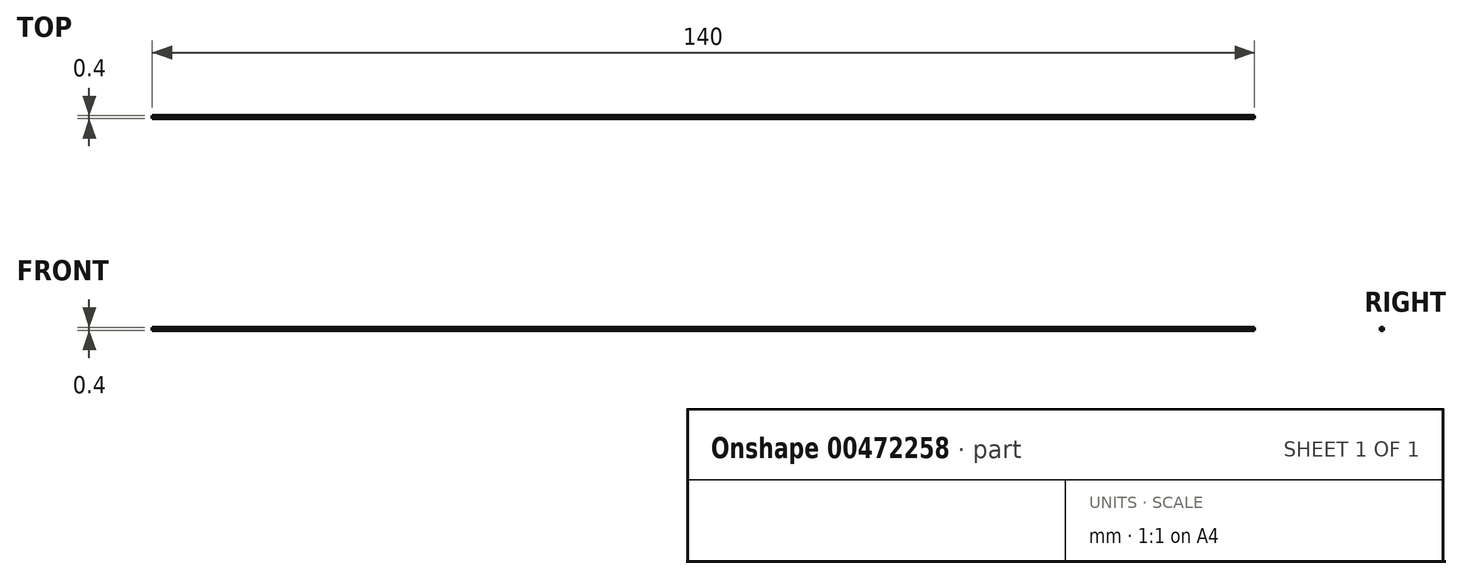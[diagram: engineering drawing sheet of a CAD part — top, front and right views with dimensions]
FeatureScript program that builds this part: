
annotation { "Feature Type Name" : "Feature", "Feature Type Description" : "" }
export const myFeature = defineFeature(function(context is Context, id is Id, definition is map)
    precondition{}
    {
        {
            var Q0;
            Q0=qCreatedBy(makeId("Top.planeOp"),FACE);
            var sketch = newSketch(context, id + "F0", { "sketchPlane" : qUnion([Q0])});
            skLineSegment(sketch, "E0.bottom", {"start": v(70, -0.2) * mm, "end": v(-70, -0.2) * mm});
            skLineSegment(sketch, "E0.top", {"start": v(70, 0.2) * mm, "end": v(-70, 0.2) * mm});
            skLineSegment(sketch, "E0.left", {"start": v(70, -0.2) * mm, "end": v(70, 0.2) * mm});
            skLineSegment(sketch, "E0.right", {"start": v(-70, -0.2) * mm, "end": v(-70, 0.2) * mm});
            skPoint(sketch, "E0.middle", {"position": v(0, 0) * mm});
            skLineSegment(sketch, "E1", {"start": v(70, -0.2) * mm, "end": v(70, -4.81) * mm});
            skLineSegment(sketch, "E2", {"start": v(70, -4.81) * mm, "end": v(72.97, -4.81) * mm});
            skLineSegment(sketch, "E3", {"start": v(72.97, -4.81) * mm, "end": v(72.97, 5.53) * mm});
            skLineSegment(sketch, "E4", {"start": v(72.97, 5.53) * mm, "end": v(70, 5.53) * mm});
            skLineSegment(sketch, "E5", {"start": v(70, 5.53) * mm, "end": v(70, 0.2) * mm});
            skLineSegment(sketch, "E6", {"start": v(-70, -0.2) * mm, "end": v(-70, -3.83) * mm});
            skLineSegment(sketch, "E7", {"start": v(-70, -3.83) * mm, "end": v(-74.12, -3.83) * mm});
            skLineSegment(sketch, "E8", {"start": v(-74.12, -3.83) * mm, "end": v(-74.12, 4.86) * mm});
            skLineSegment(sketch, "E9", {"start": v(-74.12, 4.86) * mm, "end": v(-70, 4.86) * mm});
            skLineSegment(sketch, "E10", {"start": v(-70, 4.86) * mm, "end": v(-70, 0.2) * mm});
            skSolve(sketch);
        }
        {
            var Q0;
            Q0=makeQuery(id+"F0.imprint","IMPRINT",FACE,{"disambiguationData":[TD([[makeQuery(id+"F0.imprint","IMPRINT",EDGE,{"derivedFrom":sQuery(id+"F0.wireOp",EDGE,"E0.bottom")}),-1.0]])]});
            extrude(context, id + "F1", {"entities" : qUnion([Q0]), "depth" : 0.4 * mm});
        }
    });
